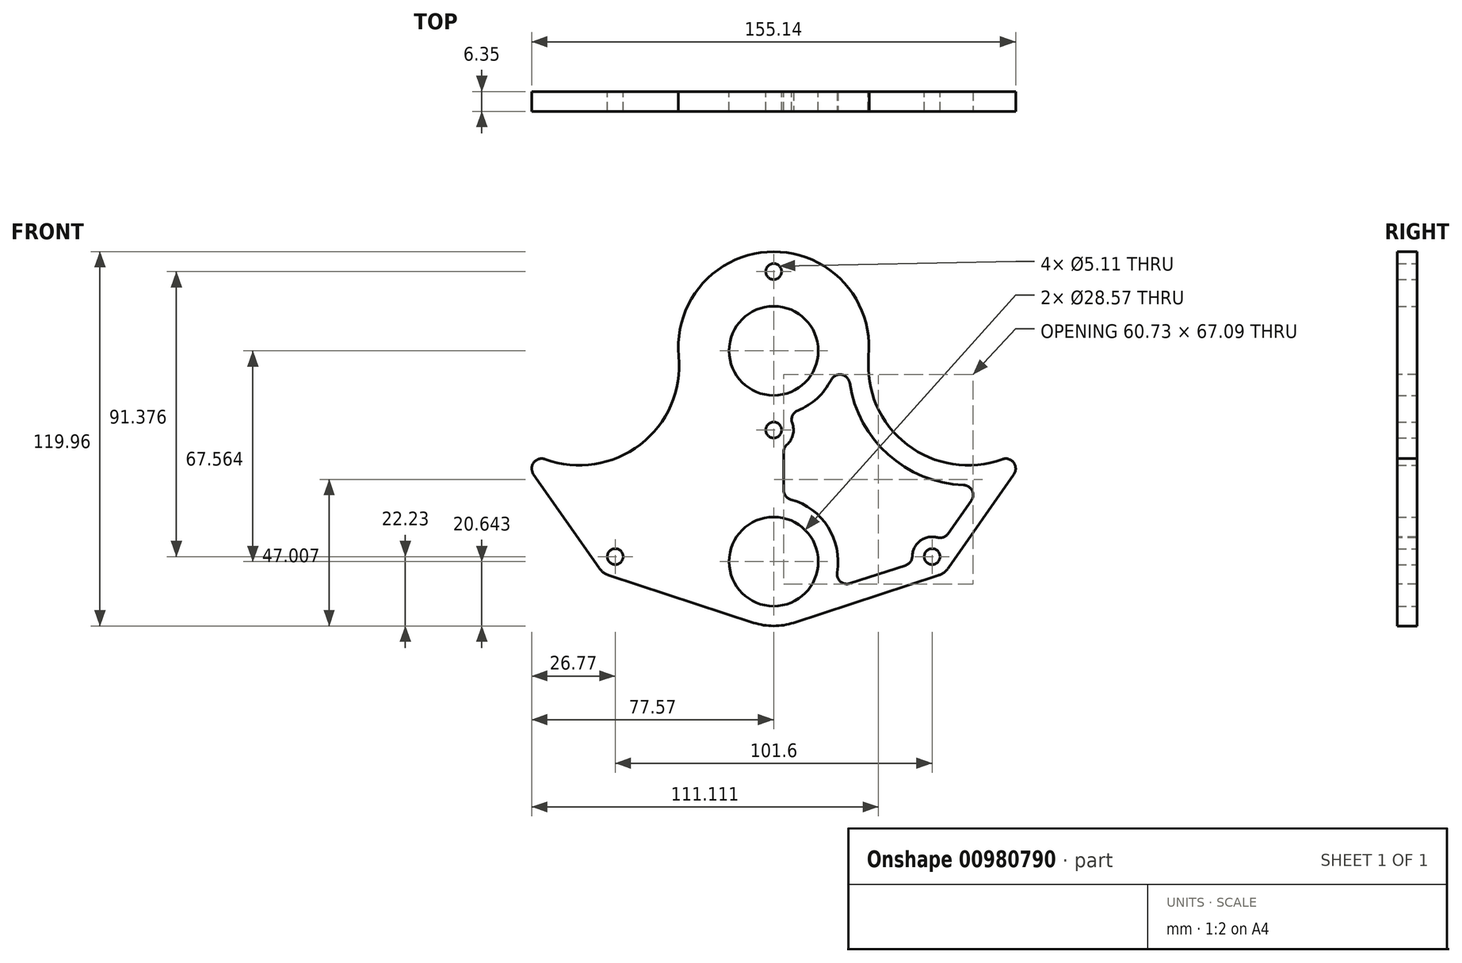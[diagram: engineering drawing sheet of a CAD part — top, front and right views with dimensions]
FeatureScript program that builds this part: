
annotation { "Feature Type Name" : "Feature", "Feature Type Description" : "" }
export const myFeature = defineFeature(function(context is Context, id is Id, definition is map)
    precondition{}
    {
        {
            var Q0;
            Q0=qCreatedBy(makeId("Front.planeOp"),FACE);
            var sketch = newSketch(context, id + "F0", { "sketchPlane" : qUnion([Q0])});
            skCircle(sketch, "E0", {"center": v(-62.3, 61.28) * mm, "radius": 32 * mm, "construction": true});
            skCircle(sketch, "E1", {"center": v(62.3, 61.28) * mm, "radius": 32 * mm, "construction": true});
            skLineSegment(sketch, "E2", {"start": v(0, 0) * mm, "end": v(0, 61.28) * mm, "construction": true});
            skLineSegment(sketch, "E3", {"start": v(-62.3, 61.28) * mm, "end": v(62.3, 61.28) * mm, "construction": true});
            skLineSegment(sketch, "E4.bottom", {"start": v(-127, 25.4) * mm, "end": v(127, 25.4) * mm, "construction": true});
            skLineSegment(sketch, "E4.top", {"start": v(-127, -25.4) * mm, "end": v(127, -25.4) * mm, "construction": true});
            skLineSegment(sketch, "E4.left", {"start": v(-127, 25.4) * mm, "end": v(-127, -25.4) * mm, "construction": true});
            skLineSegment(sketch, "E4.right", {"start": v(127, 25.4) * mm, "end": v(127, -25.4) * mm, "construction": true});
            skPoint(sketch, "E4.middle", {"position": v(0, 0) * mm});
            skCircle(sketch, "E5", {"center": v(-62.3, 61.28) * mm, "radius": 9.02 * mm, "construction": true});
            skCircle(sketch, "E6", {"center": v(62.3, 61.28) * mm, "radius": 9.02 * mm, "construction": true});
            skCircle(sketch, "E7", {"center": v(0, -1.59) * mm, "radius": 50.8 * mm, "construction": true});
            skCircle(sketch, "E8", {"center": v(-62.3, 61.28) * mm, "radius": 9.55 * mm, "construction": true});
            skCircle(sketch, "E9", {"center": v(62.3, 61.28) * mm, "radius": 9.55 * mm, "construction": true});
            skCircle(sketch, "E10", {"center": v(0, 65.98) * mm, "radius": 14.29 * mm});
            skCircle(sketch, "E11", {"center": v(0, -1.59) * mm, "radius": 14.29 * mm});
            skLineSegment(sketch, "E12", {"start": v(-88.54, 42.95) * mm, "end": v(-56, -3.64) * mm});
            skCircle(sketch, "E13", {"center": v(-114.3, 12.7) * mm, "radius": 2.55 * mm, "construction": true});
            skCircle(sketch, "E14.0.1.0", {"center": v(-114.3, -12.7) * mm, "radius": 2.55 * mm, "construction": true});
            skCircle(sketch, "E14.1.0.0", {"center": v(-88.9, 12.7) * mm, "radius": 2.55 * mm, "construction": true});
            skCircle(sketch, "E14.1.1.0", {"center": v(-88.9, -12.7) * mm, "radius": 2.55 * mm, "construction": true});
            skCircle(sketch, "E14.2.0.0", {"center": v(-63.5, 12.7) * mm, "radius": 2.55 * mm, "construction": true});
            skCircle(sketch, "E14.2.1.0", {"center": v(-63.5, -12.7) * mm, "radius": 2.55 * mm, "construction": true});
            skCircle(sketch, "E14.3.0.0", {"center": v(-38.1, 12.7) * mm, "radius": 2.55 * mm, "construction": true});
            skCircle(sketch, "E14.3.1.0", {"center": v(-38.1, -12.7) * mm, "radius": 2.55 * mm, "construction": true});
            skCircle(sketch, "E14.4.0.0", {"center": v(-12.7, 12.7) * mm, "radius": 2.55 * mm, "construction": true});
            skCircle(sketch, "E14.4.1.0", {"center": v(-12.7, -12.7) * mm, "radius": 2.55 * mm, "construction": true});
            skCircle(sketch, "E14.5.0.0", {"center": v(12.7, 12.7) * mm, "radius": 2.55 * mm, "construction": true});
            skCircle(sketch, "E14.5.1.0", {"center": v(12.7, -12.7) * mm, "radius": 2.55 * mm, "construction": true});
            skCircle(sketch, "E14.6.0.0", {"center": v(38.1, 12.7) * mm, "radius": 2.55 * mm, "construction": true});
            skCircle(sketch, "E14.6.1.0", {"center": v(38.1, -12.7) * mm, "radius": 2.55 * mm, "construction": true});
            skCircle(sketch, "E14.7.0.0", {"center": v(63.5, 12.7) * mm, "radius": 2.55 * mm, "construction": true});
            skCircle(sketch, "E14.7.1.0", {"center": v(63.5, -12.7) * mm, "radius": 2.55 * mm, "construction": true});
            skCircle(sketch, "E14.8.0.0", {"center": v(88.9, 12.7) * mm, "radius": 2.55 * mm, "construction": true});
            skCircle(sketch, "E14.8.1.0", {"center": v(88.9, -12.7) * mm, "radius": 2.55 * mm, "construction": true});
            skCircle(sketch, "E14.9.0.0", {"center": v(114.3, 12.7) * mm, "radius": 2.55 * mm, "construction": true});
            skCircle(sketch, "E14.9.1.0", {"center": v(114.3, -12.7) * mm, "radius": 2.55 * mm, "construction": true});
            skLineSegment(sketch, "E14.direction1", {"start": v(-114.3, 12.7) * mm, "end": v(-88.9, 12.7) * mm, "construction": true});
            skLineSegment(sketch, "E14.direction2", {"start": v(-114.3, 12.7) * mm, "end": v(-114.3, -12.7) * mm, "construction": true});
            skCircle(sketch, "E15", {"center": v(-50.8, 0) * mm, "radius": 2.55 * mm});
            skCircle(sketch, "E16", {"center": v(50.8, 0) * mm, "radius": 2.55 * mm});
            skCircle(sketch, "E17", {"center": v(-50.8, 0) * mm, "radius": 6.35 * mm, "construction": true});
            skCircle(sketch, "E18", {"center": v(50.8, 0) * mm, "radius": 6.35 * mm, "construction": true});
            skArc(sketch, "E19", {"start": v(-56, -3.64) * mm, "mid": v(-54.59, -5.1) * mm, "end": v(-52.77, -6.04) * mm});
            skArc(sketch, "E20", {"start": v(52.77, -6.04) * mm, "mid": v(54.59, -5.1) * mm, "end": v(56, -3.64) * mm});
            skLineSegment(sketch, "E21", {"start": v(56, -3.64) * mm, "end": v(88.54, 42.95) * mm});
            skLineSegment(sketch, "E22", {"start": v(-75, 39.28) * mm, "end": v(-62.3, 61.28) * mm, "construction": true});
            skLineSegment(sketch, "E23", {"start": v(-62.3, 61.28) * mm, "end": v(-49.6, 83.27) * mm, "construction": true});
            skCircle(sketch, "E24", {"center": v(-75, 39.28) * mm, "radius": 2.55 * mm, "construction": true});
            skCircle(sketch, "E25", {"center": v(-49.6, 83.27) * mm, "radius": 2.55 * mm, "construction": true});
            skLineSegment(sketch, "E26.MirrorCS", {"start": v(75, 39.28) * mm, "end": v(62.3, 61.28) * mm, "construction": true});
            skCircle(sketch, "E27.MirrorC", {"center": v(75, 39.28) * mm, "radius": 2.55 * mm, "construction": true});
            skLineSegment(sketch, "E28.MirrorCS", {"start": v(62.3, 61.28) * mm, "end": v(49.6, 83.27) * mm, "construction": true});
            skCircle(sketch, "E29.MirrorC", {"center": v(49.6, 83.27) * mm, "radius": 2.55 * mm, "construction": true});
            skCircle(sketch, "E30", {"center": v(0, 65.98) * mm, "radius": 53.47 * mm, "construction": true});
            skCircle(sketch, "E31", {"center": v(0, 65.98) * mm, "radius": 25.4 * mm, "construction": true});
            skLineSegment(sketch, "E32", {"start": v(-52.77, -6.04) * mm, "end": v(-6.42, -21.2) * mm});
            skCircle(sketch, "E33", {"center": v(0, -1.59) * mm, "radius": 20.64 * mm, "construction": true});
            skArc(sketch, "E34", {"start": v(-6.42, -21.2) * mm, "mid": v(0, -22.22) * mm, "end": v(6.42, -21.2) * mm});
            skLineSegment(sketch, "E35", {"start": v(52.77, -6.04) * mm, "end": v(6.42, -21.2) * mm});
            skCircle(sketch, "E36", {"center": v(0, 65.98) * mm, "radius": 56 * mm, "construction": true});
            skCircle(sketch, "E37", {"center": v(0, 91.38) * mm, "radius": 2.55 * mm});
            skCircle(sketch, "E38", {"center": v(0, 40.58) * mm, "radius": 2.55 * mm});
            skLineSegment(sketch, "E39", {"start": v(0, 40.58) * mm, "end": v(0, 65.98) * mm, "construction": true});
            skLineSegment(sketch, "E40", {"start": v(0, 65.98) * mm, "end": v(0, 91.38) * mm, "construction": true});
            skCircle(sketch, "E41", {"center": v(0, -1.59) * mm, "radius": 41.91 * mm, "construction": true});
            skCircle(sketch, "E42", {"center": v(0, -1.59) * mm, "radius": 44.45 * mm, "construction": true});
            skArc(sketch, "E43", {"start": v(-88.54, 42.95) * mm, "mid": v(-51.28, 31.23) * mm, "end": v(-30.44, 64.28) * mm});
            skArc(sketch, "E44", {"start": v(30.44, 64.28) * mm, "mid": v(51.28, 31.23) * mm, "end": v(88.54, 42.95) * mm});
            skArc(sketch, "E45", {"start": v(30.44, 64.28) * mm, "mid": v(0, 97.73) * mm, "end": v(-30.44, 64.28) * mm});
            skCircle(sketch, "E46", {"center": v(0, 91.38) * mm, "radius": 6.35 * mm, "construction": true});
            skSolve(sketch);
        }
        {
            var Q0;
            Q0=qSketchRegion(id+"F0",true);
            extrude(context, id + "F1", {"entities" : qUnion([Q0]), "depth" : 6.35 * mm, "offsetDistance" : 25.4 * mm});
        }
        {
            var Q0;
            Q0=makeQuery(id+"F1.opExtrude","SWEPT_EDGE",EDGE,{"disambiguationData":[OSD([sQuery(id+"F0.wireOp",EDGE,"E12"),sQuery(id+"F0.wireOp",EDGE,"E43")])]});
            var Q1;
            Q1=makeQuery(id+"F1.opExtrude","SWEPT_EDGE",EDGE,{"disambiguationData":[OSD([sQuery(id+"F0.wireOp",EDGE,"E21"),sQuery(id+"F0.wireOp",EDGE,"E44")])]});
            fillet(context, id + "F2", {"entities" : qUnion([Q0, Q1]), "radius" : 3.17 * mm, "tangentPropagation" : true, "allowEdgeOverflow" : false});
        }
        {
            var Q0;
            Q0=makeQuery(id+"F1.opExtrude","CAP_FACE",FACE,{"disambiguationData":[OSD([sQuery(id+"F0.wireOp",EDGE,"E10"),sQuery(id+"F0.wireOp",EDGE,"E11"),sQuery(id+"F0.wireOp",EDGE,"E12"),sQuery(id+"F0.wireOp",EDGE,"E15"),sQuery(id+"F0.wireOp",EDGE,"E16"),sQuery(id+"F0.wireOp",EDGE,"E19"),sQuery(id+"F0.wireOp",EDGE,"E20"),sQuery(id+"F0.wireOp",EDGE,"E21"),sQuery(id+"F0.wireOp",EDGE,"E32"),sQuery(id+"F0.wireOp",EDGE,"E34"),sQuery(id+"F0.wireOp",EDGE,"E35"),sQuery(id+"F0.wireOp",EDGE,"E37"),sQuery(id+"F0.wireOp",EDGE,"E38"),sQuery(id+"F0.wireOp",EDGE,"E43"),sQuery(id+"F0.wireOp",EDGE,"E44"),sQuery(id+"F0.wireOp",EDGE,"E45")])],"isStart":false});
            var sketch = newSketch(context, id + "F3", { "sketchPlane" : qUnion([Q0])});
            skArc(sketch, "E47.0", {"start": v(24.12, 64.87) * mm, "mid": v(35.58, 33.77) * mm, "end": v(67.01, 23.21) * mm, "construction": true});
            skLineSegment(sketch, "E47.1", {"start": v(50.8, 0) * mm, "end": v(67.01, 23.21) * mm, "construction": true});
            skArc(sketch, "E47.2", {"start": v(24.12, 64.87) * mm, "mid": v(0, 91.38) * mm, "end": v(-24.12, 64.87) * mm, "construction": true});
            skLineSegment(sketch, "E47.3", {"start": v(50.8, 0) * mm, "end": v(4.44, -15.17) * mm, "construction": true});
            skArc(sketch, "E47.4", {"start": v(-67.01, 23.21) * mm, "mid": v(-35.58, 33.77) * mm, "end": v(-24.12, 64.87) * mm, "construction": true});
            skLineSegment(sketch, "E47.5", {"start": v(-67.01, 23.21) * mm, "end": v(-50.8, 0) * mm, "construction": true});
            skLineSegment(sketch, "E47.6", {"start": v(-50.8, 0) * mm, "end": v(-4.44, -15.17) * mm, "construction": true});
            skArc(sketch, "E47.7", {"start": v(-4.44, -15.17) * mm, "mid": v(0, -15.88) * mm, "end": v(4.44, -15.17) * mm, "construction": true});
            skCircle(sketch, "E48", {"center": v(0, 91.38) * mm, "radius": 6.35 * mm, "construction": true});
            skCircle(sketch, "E49", {"center": v(0, 40.58) * mm, "radius": 6.35 * mm, "construction": true});
            skCircle(sketch, "E50", {"center": v(-50.8, 0) * mm, "radius": 6.35 * mm, "construction": true});
            skCircle(sketch, "E51", {"center": v(50.8, 0) * mm, "radius": 6.35 * mm, "construction": true});
            skCircle(sketch, "E52", {"center": v(0, 65.98) * mm, "radius": 20.64 * mm, "construction": true});
            skCircle(sketch, "E53", {"center": v(0, -1.59) * mm, "radius": 20.64 * mm, "construction": true});
            skLineSegment(sketch, "E54", {"start": v(-50.8, 0) * mm, "end": v(0, 40.58) * mm, "construction": true});
            skLineSegment(sketch, "E55", {"start": v(0, 40.58) * mm, "end": v(0, 0) * mm, "construction": true});
            skLineSegment(sketch, "E56", {"start": v(3.17, 18.8) * mm, "end": v(3.17, 35.08) * mm});
            skArc(sketch, "E57", {"start": v(18.6, -10.54) * mm, "mid": v(18.27, 8.01) * mm, "end": v(3.18, 18.8) * mm});
            skLineSegment(sketch, "E58", {"start": v(18.6, -10.54) * mm, "end": v(44.76, -1.97) * mm});
            skArc(sketch, "E59", {"start": v(48.47, 5.9) * mm, "mid": v(45.05, 2.7) * mm, "end": v(44.76, -1.97) * mm});
            skArc(sketch, "E60", {"start": v(3.18, 35.08) * mm, "mid": v(6.34, 40.22) * mm, "end": v(3.77, 45.69) * mm});
            skArc(sketch, "E61", {"start": v(3.77, 45.69) * mm, "mid": v(12.36, 49.45) * mm, "end": v(18.4, 56.62) * mm});
            skArc(sketch, "E62", {"start": v(54.44, 5.2) * mm, "mid": v(51.54, 6.3) * mm, "end": v(48.47, 5.9) * mm});
            skLineSegment(sketch, "E63", {"start": v(54.44, 5.2) * mm, "end": v(67.01, 23.21) * mm});
            skArc(sketch, "E64", {"start": v(24.37, 55.65) * mm, "mid": v(39.09, 30.75) * mm, "end": v(67.01, 23.21) * mm});
            skArc(sketch, "E65", {"start": v(24.37, 55.65) * mm, "mid": v(21.74, 58.32) * mm, "end": v(18.4, 56.62) * mm});
            skSolve(sketch);
        }
        {
            var Q0;
            Q0 = qSketchRegion(id + "F3", true);
            extrude(context, id + "F4", {"entities" : qUnion([Q0]), "operationType" : NewBodyOperationType.REMOVE, "oppositeDirection" : true, "depth" : 25.4 * mm, "offsetDistance" : 25.4 * mm});
        }
        {
            var Q0;
            Q0=makeQuery(id+"F4.boolean.opBoolean","COPY",EDGE,{"derivedFrom":makeQuery(id+"F4.opExtrude","SWEPT_EDGE",EDGE,{"disambiguationData":[OSD([sQuery(id+"F3.wireOp",EDGE,"E60"),sQuery(id+"F3.wireOp",EDGE,"E61")])]})});
            var Q1;
            Q1=makeQuery(id+"F4.boolean.opBoolean","COPY",EDGE,{"derivedFrom":makeQuery(id+"F4.opExtrude","SWEPT_EDGE",EDGE,{"disambiguationData":[OSD([sQuery(id+"F3.wireOp",EDGE,"E56"),sQuery(id+"F3.wireOp",EDGE,"E60")])]})});
            var Q2;
            Q2=makeQuery(id+"F4.boolean.opBoolean","COPY",EDGE,{"derivedFrom":makeQuery(id+"F4.opExtrude","SWEPT_EDGE",EDGE,{"disambiguationData":[OSD([sQuery(id+"F3.wireOp",EDGE,"E56"),sQuery(id+"F3.wireOp",EDGE,"E57")])]})});
            var Q3;
            Q3=makeQuery(id+"F4.boolean.opBoolean","COPY",EDGE,{"derivedFrom":makeQuery(id+"F4.opExtrude","SWEPT_EDGE",EDGE,{"disambiguationData":[OSD([sQuery(id+"F3.wireOp",EDGE,"E57"),sQuery(id+"F3.wireOp",EDGE,"E58")])]})});
            var Q4;
            Q4=makeQuery(id+"F4.boolean.opBoolean","COPY",EDGE,{"derivedFrom":makeQuery(id+"F4.opExtrude","SWEPT_EDGE",EDGE,{"disambiguationData":[OSD([sQuery(id+"F3.wireOp",EDGE,"E58"),sQuery(id+"F3.wireOp",EDGE,"E59")])]})});
            var Q5;
            Q5=makeQuery(id+"F4.boolean.opBoolean","COPY",EDGE,{"derivedFrom":makeQuery(id+"F4.opExtrude","SWEPT_EDGE",EDGE,{"disambiguationData":[OSD([sQuery(id+"F3.wireOp",EDGE,"E62"),sQuery(id+"F3.wireOp",EDGE,"E63")])]})});
            var Q6;
            Q6=makeQuery(id+"F4.boolean.opBoolean","COPY",EDGE,{"derivedFrom":makeQuery(id+"F4.opExtrude","SWEPT_EDGE",EDGE,{"disambiguationData":[OSD([sQuery(id+"F3.wireOp",EDGE,"E63"),sQuery(id+"F3.wireOp",EDGE,"E64")])]})});
            fillet(context, id + "F5", {"entities" : qUnion([Q0, Q1, Q2, Q3, Q4, Q5, Q6]), "radius" : 3.17 * mm, "tangentPropagation" : true, "allowEdgeOverflow" : false});
        }
    });
